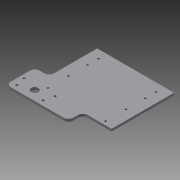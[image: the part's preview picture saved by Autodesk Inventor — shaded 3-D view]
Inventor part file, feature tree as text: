
AUTODESK INVENTOR PART (.ipt)
format: ipt  version: 2013 (Build 170138000, 138)  size: 192,512 bytes
history: native  units: in
note: dims shown in document units (in); Inventor stores cm internally (conversion verified against a paired STEP export)
features: hole x3, sketch x3, other x2, sheet_metal_op x1
ambient origin geometry x8: Origin, YZ Plane, XZ Plane, XY Plane, X Axis, Y Axis, Z Axis, Center Point
feature tree (9):
  sheet_metal_op  "Face2"
  hole  "Hole2"  [1 undecoded]
  hole  "Hole3"  [1 undecoded]
  hole  "Hole5"  [1 undecoded]
  other  "Plate2"
  sketch  "Sketch5"  dims[d15=0.25in d16=0.25in]
  sketch  "Sketch12"  dims[d27=1.0in d28=1.0in]
  sketch  "Sketch14"  dims[d30=5.25in d31=0.196in d32=0.75in d33=0.375in d34=0.25in d35=0.5635in d36=1.0in d37=0.8108in d62=0.875in d64=1.5in d67=0.5in d69=0.5in d89=2.0in d90=2.0in d91=1.0in d93=6.0in d94=1.0in d97=0.75in d98=0.75in d99=0.375in d100=0.25in d101=0.5635in d102=0.25in d103=0.8108in d105=3.0in d106=0.5in d107=2.0in d108=8.0in d109=5.0in d110=6.5in d111=1.5in d129=2.0in d130=0.25in d135=0.25in d136=1.0in d137=0.5in d138=3.25in d139=1.625in d140=0.25in d141=0.75in d142=0.375in d143=0.25in d144=0.5635in d145=0.25in d146=0.8108in]
  other  "Definition1"
note: 3 required parameter values undecoded (feature->parameter linkage not recoverable at this tier; creation-order binding heuristic only, values carry confidence <= 0.55)
